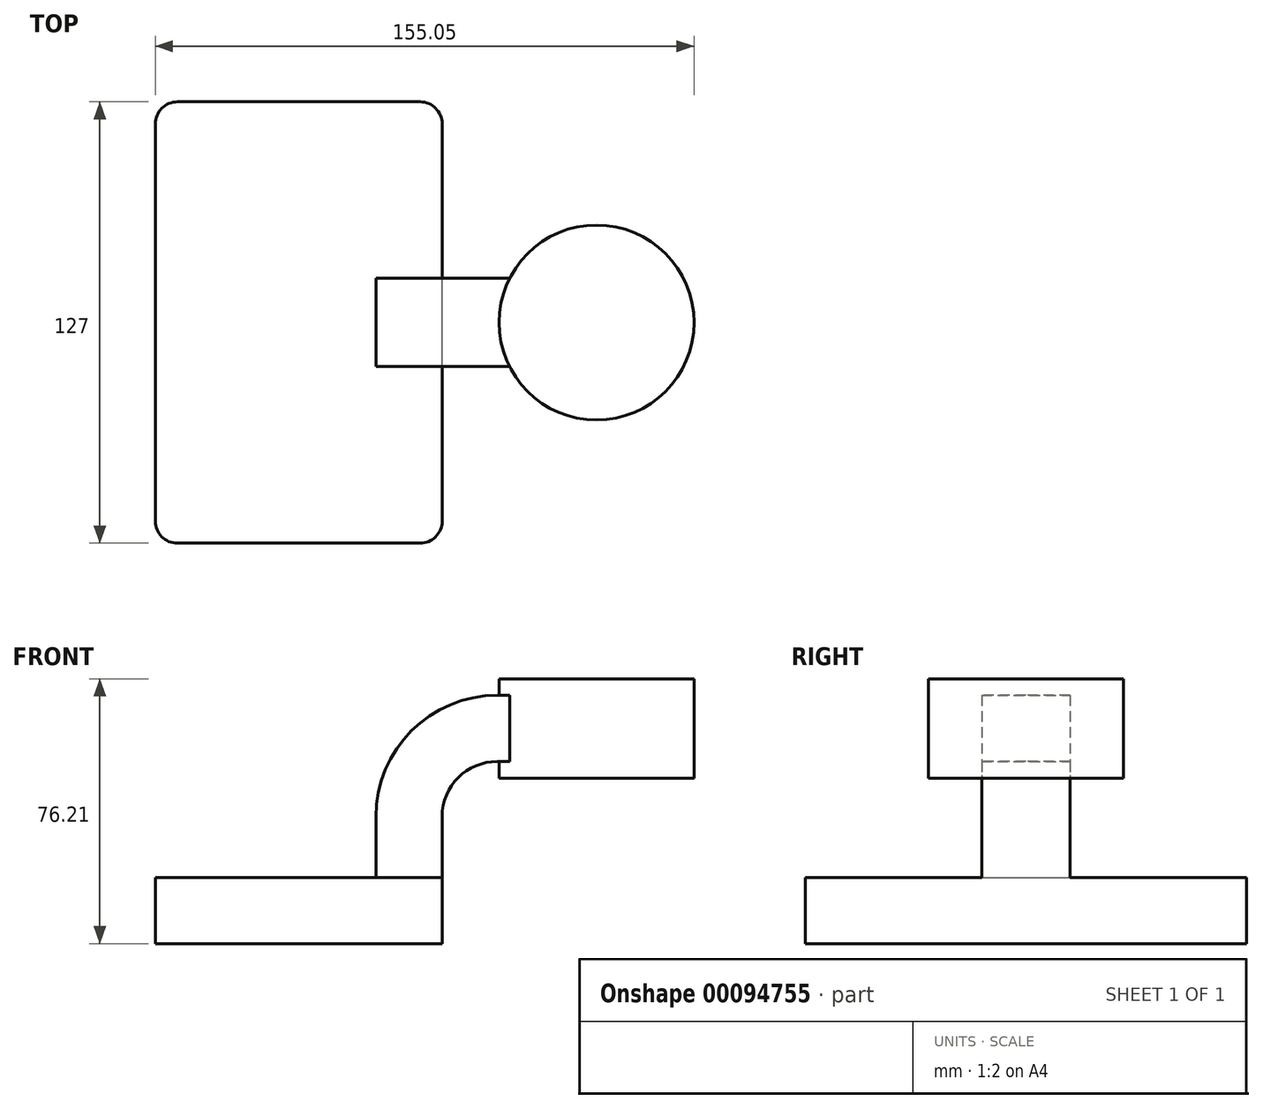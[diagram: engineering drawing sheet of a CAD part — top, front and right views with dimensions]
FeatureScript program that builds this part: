
annotation { "Feature Type Name" : "Feature", "Feature Type Description" : "" }
export const myFeature = defineFeature(function(context is Context, id is Id, definition is map)
    precondition{}
    {
        {
            var Q0;
            Q0=qCreatedBy(makeId("Front.planeOp"),FACE);
            var sketch = newSketch(context, id + "F0", { "sketchPlane" : qUnion([Q0])});
            skLineSegment(sketch, "E0.bottom", {"start": v(41.28, -9.52) * mm, "end": v(-41.27, -9.53) * mm});
            skLineSegment(sketch, "E0.top", {"start": v(41.27, 9.53) * mm, "end": v(-41.28, 9.53) * mm});
            skLineSegment(sketch, "E0.left", {"start": v(41.28, -9.52) * mm, "end": v(41.28, 9.53) * mm});
            skLineSegment(sketch, "E0.right", {"start": v(-41.27, -9.53) * mm, "end": v(-41.28, 9.53) * mm});
            skPoint(sketch, "E0.middle", {"position": v(0, 0) * mm});
            skLineSegment(sketch, "E1.bottom", {"start": v(62.98, 66.68) * mm, "end": v(113.78, 66.68) * mm});
            skLineSegment(sketch, "E1.top", {"start": v(62.98, 38.1) * mm, "end": v(113.78, 38.1) * mm});
            skLineSegment(sketch, "E1.left", {"start": v(62.98, 66.68) * mm, "end": v(62.98, 38.1) * mm});
            skLineSegment(sketch, "E1.right", {"start": v(113.78, 66.68) * mm, "end": v(113.78, 38.1) * mm});
            skLineSegment(sketch, "E2", {"start": v(41.27, 9.53) * mm, "end": v(41.27, 27) * mm});
            skArc(sketch, "E3", {"start": v(41.27, 27) * mm, "mid": v(45.92, 38.23) * mm, "end": v(57.15, 42.88) * mm});
            skLineSegment(sketch, "E4", {"start": v(57.15, 42.88) * mm, "end": v(85.73, 42.88) * mm});
            skLineSegment(sketch, "E5.0", {"start": v(57.15, 61.93) * mm, "end": v(85.73, 61.93) * mm});
            skArc(sketch, "E5.1", {"start": v(22.23, 27) * mm, "mid": v(32.45, 51.7) * mm, "end": v(57.15, 61.93) * mm});
            skLineSegment(sketch, "E5.2", {"start": v(22.22, 9.53) * mm, "end": v(22.22, 27) * mm});
            skLineSegment(sketch, "E6", {"start": v(85.73, 38.1) * mm, "end": v(85.73, 66.68) * mm});
            skFitSpline(sketch, "E7", {"points": [v(-41.28, 9.53) * mm, v(57.15, 61.93) * mm], "startDerivative": vector(11.98, 92.87) * mm, "endDerivative": vector(48.98, -8.53) * mm});
            skSolve(sketch);
        }
        {
            var Q0;
            Q0=makeQuery(id+"F0.imprint","IMPRINT",FACE,{"disambiguationData":[TD([[makeQuery(id+"F0.imprint","IMPRINT",EDGE,{"derivedFrom":sQuery(id+"F0.wireOp",EDGE,"E0.bottom")}),-1.0]])]});
            extrude(context, id + "F1", {"entities" : qUnion([Q0]), "endBound" : BoundingType.SYMMETRIC, "depth" : 127 * mm});
        }
        {
            var Q0;
            {var subQ1=sQuery(id+"F0.wireOp",EDGE,"E2");Q0=makeQuery(id+"F0.imprint","IMPRINT",FACE,{"disambiguationData":[TD([[makeQuery(id+"F0.imprint","IMPRINT",EDGE,{"derivedFrom":subQ1}),1.0]])]});}
            var Q1;
            {var subQ0=sQuery(id+"F0.wireOp",EDGE,"E5.0");var subQ1=sQuery(id+"F0.wireOp",EDGE,"E1.left");var subQ2=makeQuery(id+"F0.imprint","INTERSECT",VERTEX,{"derivedFrom":[subQ1,subQ0]});Q1=makeQuery(id+"F0.imprint","IMPRINT",FACE,{"disambiguationData":[TD([[makeQuery(id+"F0.imprint","IMPRINT",EDGE,{"disambiguationData":[TD([[subQ2,-1.0]])],"derivedFrom":subQ1}),1.0]])]});}
            extrude(context, id + "F2", {"entities" : qUnion([Q0, Q1]), "operationType" : NewBodyOperationType.ADD, "endBound" : BoundingType.SYMMETRIC, "depth" : 25.4 * mm});
        }
        {
            var Q0;
            Q0=makeQuery(id+"F0.imprint","IMPRINT",FACE,{"disambiguationData":[TD([[makeQuery(id+"F0.imprint","IMPRINT",EDGE,{"derivedFrom":sQuery(id+"F0.wireOp",EDGE,"E5.1")}),1.0]])]});
            extrude(context, id + "F3", {"entities" : qUnion([Q0]), "operationType" : NewBodyOperationType.ADD, "endBound" : BoundingType.SYMMETRIC, "depth" : 15.88 * mm});
        }
        {
            var Q0;
            {var subQ0=sQuery(id+"F0.wireOp",EDGE,"E1.right");Q0=makeQuery(id+"F0.imprint","IMPRINT",FACE,{"disambiguationData":[TD([[makeQuery(id+"F0.imprint","IMPRINT",EDGE,{"derivedFrom":subQ0}),-1.0]])]});}
            var Q1;
            Q1=sQuery(id+"F0.wireOp",EDGE,"E6");
            revolve(context, id + "F4", {"operationType" : NewBodyOperationType.ADD, "entities" : qUnion([Q0]), "axis" : qUnion([Q1]), "revolveType" : RevolveType.FULL});
        }
        {
            var Q0;
            Q0=makeQuery(id+"F1.opExtrude","CAP_EDGE",EDGE,{"disambiguationData":[OSD([sQuery(id+"F0.wireOp",EDGE,"E0.left")])],"isStart":false});
            var Q1;
            Q1=makeQuery(id+"F1.opExtrude","CAP_EDGE",EDGE,{"disambiguationData":[OSD([sQuery(id+"F0.wireOp",EDGE,"E0.left")])],"isStart":true});
            var Q2;
            Q2=makeQuery(id+"F1.opExtrude","CAP_EDGE",EDGE,{"disambiguationData":[OSD([sQuery(id+"F0.wireOp",EDGE,"E0.right")])],"isStart":false});
            var Q3;
            Q3=makeQuery(id+"F1.opExtrude","CAP_EDGE",EDGE,{"disambiguationData":[OSD([sQuery(id+"F0.wireOp",EDGE,"E0.right")])],"isStart":true});
            fillet(context, id + "F5", {"entities" : qUnion([Q0, Q1, Q2, Q3]), "radius" : 6.35 * mm, "tangentPropagation" : true, "allowEdgeOverflow" : false});
        }
    });
